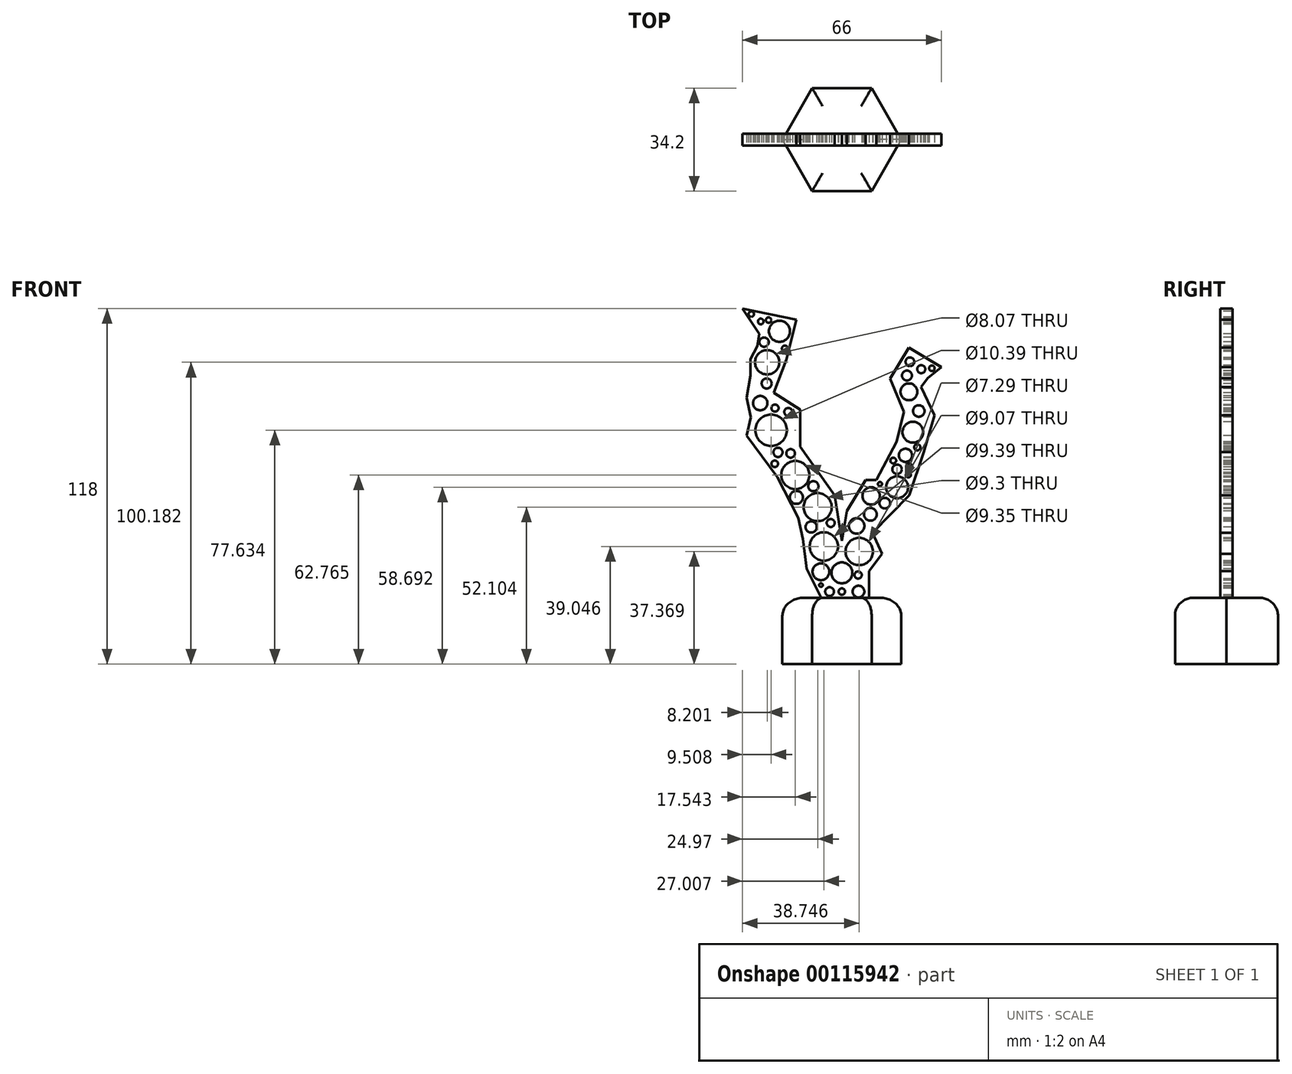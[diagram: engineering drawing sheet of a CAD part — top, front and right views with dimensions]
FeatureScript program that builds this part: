
annotation { "Feature Type Name" : "Feature", "Feature Type Description" : "" }
export const myFeature = defineFeature(function(context is Context, id is Id, definition is map)
    precondition{}
    {
        {
            var Q0;
            Q0=qCreatedBy(makeId("Top.planeOp"),FACE);
            var sketch = newSketch(context, id + "F0", { "sketchPlane" : qUnion([Q0])});
            skCircle(sketch, "E0.cCircle", {"center": v(0, 0) * mm, "radius": 17.1 * mm, "construction": true});
            skLineSegment(sketch, "E0.0", {"start": v(-9.87, 17.1) * mm, "end": v(9.87, 17.1) * mm});
            skLineSegment(sketch, "E0.1", {"start": v(9.87, 17.1) * mm, "end": v(19.74, 0) * mm});
            skLineSegment(sketch, "E0.2", {"start": v(19.74, 0) * mm, "end": v(9.87, -17.1) * mm});
            skLineSegment(sketch, "E0.3", {"start": v(9.87, -17.1) * mm, "end": v(-9.87, -17.1) * mm});
            skLineSegment(sketch, "E0.4", {"start": v(-9.87, -17.1) * mm, "end": v(-19.74, 0) * mm});
            skLineSegment(sketch, "E0.5", {"start": v(-19.74, 0) * mm, "end": v(-9.87, 17.1) * mm});
            skPoint(sketch, "E0.0.midPoint", {"position": v(0, 17.1) * mm});
            skSolve(sketch);
        }
        {
            var Q0;
            Q0 = qSketchRegion(id + "F0", true);
            extrude(context, id + "F1", {"entities" : qUnion([Q0]), "depth" : 22 * mm});
        }
        {
            var Q0;
            Q0=makeQuery(id+"F1.opExtrude","CAP_FACE",FACE,{"disambiguationData":[OSD([sQuery(id+"F0.wireOp",EDGE,"E0.0"),sQuery(id+"F0.wireOp",EDGE,"E0.1"),sQuery(id+"F0.wireOp",EDGE,"E0.2"),sQuery(id+"F0.wireOp",EDGE,"E0.3"),sQuery(id+"F0.wireOp",EDGE,"E0.4"),sQuery(id+"F0.wireOp",EDGE,"E0.5")])],"isStart":false});
            fillet(context, id + "F2", {"entities" : qUnion([Q0]), "radius" : 6 * mm, "tangentPropagation" : true, "allowEdgeOverflow" : false});
        }
        {
            var Q0;
            Q0=makeQuery(id+"F1.opExtrude","CAP_FACE",FACE,{"disambiguationData":[OSD([sQuery(id+"F0.wireOp",EDGE,"E0.0"),sQuery(id+"F0.wireOp",EDGE,"E0.1"),sQuery(id+"F0.wireOp",EDGE,"E0.2"),sQuery(id+"F0.wireOp",EDGE,"E0.3"),sQuery(id+"F0.wireOp",EDGE,"E0.4"),sQuery(id+"F0.wireOp",EDGE,"E0.5")])],"isStart":false});
            var sketch = newSketch(context, id + "F3", { "sketchPlane" : qUnion([Q0])});
            skLineSegment(sketch, "E1.bottom", {"start": v(-33, 2) * mm, "end": v(33, 2) * mm});
            skLineSegment(sketch, "E1.top", {"start": v(-33, -2) * mm, "end": v(33, -2) * mm});
            skLineSegment(sketch, "E1.left", {"start": v(-33, 2) * mm, "end": v(-33, -2) * mm});
            skLineSegment(sketch, "E1.right", {"start": v(33, 2) * mm, "end": v(33, -2) * mm});
            skPoint(sketch, "E1.middle", {"position": v(0, 0) * mm});
            skSolve(sketch);
        }
        {
            var Q0;
            Q0 = qSketchRegion(id + "F3", true);
            extrude(context, id + "F4", {"entities" : qUnion([Q0]), "operationType" : NewBodyOperationType.ADD, "depth" : 96 * mm});
        }
        {
            var Q0;
            Q0=makeQuery(id+"F4.opExtrude","SWEPT_FACE",FACE,{"disambiguationData":[OSD([sQuery(id+"F3.wireOp",EDGE,"E1.top")])]});
            var sketch = newSketch(context, id + "F5", { "sketchPlane" : qUnion([Q0])});
            skCircle(sketch, "E2", {"center": v(-15.46, 62.77) * mm, "radius": 4.67 * mm});
            skCircle(sketch, "E3", {"center": v(-8.03, 52.1) * mm, "radius": 4.65 * mm});
            skCircle(sketch, "E4", {"center": v(-6, 39.05) * mm, "radius": 4.7 * mm});
            skCircle(sketch, "E5", {"center": v(5.75, 37.37) * mm, "radius": 4.53 * mm});
            skCircle(sketch, "E6", {"center": v(4.9, 45.87) * mm, "radius": 2.58 * mm});
            skCircle(sketch, "E7", {"center": v(9.46, 49.7) * mm, "radius": 2.12 * mm});
            skCircle(sketch, "E8", {"center": v(9.7, 55.82) * mm, "radius": 2.88 * mm});
            skCircle(sketch, "E9", {"center": v(18.32, 58.7) * mm, "radius": 3.64 * mm});
            skCircle(sketch, "E10", {"center": v(18.32, 64.68) * mm, "radius": 1.56 * mm});
            skCircle(sketch, "E11", {"center": v(14.25, 53.42) * mm, "radius": 1.78 * mm});
            skCircle(sketch, "E12", {"center": v(-3.72, 46.83) * mm, "radius": 1.32 * mm});
            skCircle(sketch, "E13", {"center": v(-10.19, 45.52) * mm, "radius": 1.86 * mm});
            skCircle(sketch, "E14", {"center": v(-9.47, 59.05) * mm, "radius": 1.68 * mm});
            skCircle(sketch, "E15", {"center": v(-15.1, 55.34) * mm, "radius": 2.16 * mm});
            skCircle(sketch, "E16", {"center": v(-22.28, 66.48) * mm, "radius": 1.08 * mm});
            skCircle(sketch, "E17", {"center": v(-17.01, 69.95) * mm, "radius": 1.45 * mm});
            skCircle(sketch, "E18", {"center": v(-6.95, 30.66) * mm, "radius": 2.79 * mm});
            skCircle(sketch, "E19", {"center": v(0, 30.3) * mm, "radius": 3.46 * mm});
            skCircle(sketch, "E20", {"center": v(5.5, 24.07) * mm, "radius": 1.95 * mm});
            skCircle(sketch, "E21", {"center": v(5.39, 29.58) * mm, "radius": 1.2 * mm});
            skCircle(sketch, "E22", {"center": v(-4.08, 24.07) * mm, "radius": 1.46 * mm});
            skCircle(sketch, "E23", {"center": v(0, 24.07) * mm, "radius": 1.08 * mm});
            skCircle(sketch, "E24", {"center": v(-6.95, 26.23) * mm, "radius": 0.6 * mm});
            skLineSegment(sketch, "E25", {"start": v(-6.83, 22) * mm, "end": v(-11.66, 31.63) * mm});
            skLineSegment(sketch, "E26", {"start": v(-11.66, 31.63) * mm, "end": v(-12.94, 41.57) * mm});
            skLineSegment(sketch, "E27", {"start": v(-12.94, 41.57) * mm, "end": v(-14.5, 48.52) * mm});
            skLineSegment(sketch, "E28", {"start": v(-14.5, 48.52) * mm, "end": v(-21.45, 62.17) * mm});
            skLineSegment(sketch, "E29", {"start": v(-21.45, 62.17) * mm, "end": v(-31.63, 75.83) * mm});
            skLineSegment(sketch, "E30", {"start": v(10.18, 43.6) * mm, "end": v(13.3, 36.65) * mm});
            skLineSegment(sketch, "E31", {"start": v(13.3, 36.65) * mm, "end": v(8.98, 30.9) * mm});
            skLineSegment(sketch, "E32", {"start": v(8.98, 30.9) * mm, "end": v(8.98, 22) * mm});
            skCircle(sketch, "E33", {"center": v(-20.71, 110.48) * mm, "radius": 3.5 * mm});
            skCircle(sketch, "E34", {"center": v(-24.8, 100.18) * mm, "radius": 4.04 * mm});
            skCircle(sketch, "E35", {"center": v(-23.5, 77.63) * mm, "radius": 5.2 * mm});
            skCircle(sketch, "E36", {"center": v(-27.09, 86.62) * mm, "radius": 2.38 * mm});
            skCircle(sketch, "E37", {"center": v(21.11, 69.3) * mm, "radius": 2.2 * mm});
            skCircle(sketch, "E38", {"center": v(23.57, 76.98) * mm, "radius": 3.45 * mm});
            skCircle(sketch, "E39", {"center": v(22.26, 90.38) * mm, "radius": 2.8 * mm});
            skCircle(sketch, "E40", {"center": v(22.59, 100.35) * mm, "radius": 1.46 * mm});
            skCircle(sketch, "E41", {"center": v(26.34, 97.9) * mm, "radius": 1.35 * mm});
            skCircle(sketch, "E42", {"center": v(21.6, 95.77) * mm, "radius": 1.63 * mm});
            skCircle(sketch, "E43", {"center": v(25.53, 84) * mm, "radius": 1.91 * mm});
            skCircle(sketch, "E44", {"center": v(-24.96, 93.16) * mm, "radius": 1.67 * mm});
            skCircle(sketch, "E45", {"center": v(-17.77, 83.68) * mm, "radius": 1.35 * mm});
            skCircle(sketch, "E46", {"center": v(-21.2, 70.28) * mm, "radius": 1.52 * mm});
            skCircle(sketch, "E47", {"center": v(-22.18, 84.99) * mm, "radius": 1.19 * mm});
            skCircle(sketch, "E48", {"center": v(-18.92, 104.76) * mm, "radius": 0.98 * mm});
            skPoint(sketch, "E49.endSnap0", {"position": v(-11.68, 104.81) * mm});
            skPoint(sketch, "E50.orphan", {"position": v(-8.27, 100.32) * mm});
            skPoint(sketch, "E49.end.orphan", {"position": v(-11.68, 96.42) * mm});
            skPoint(sketch, "E51.end.orphan", {"position": v(0, 40.87) * mm});
            skLineSegment(sketch, "E52", {"start": v(0, 40.87) * mm, "end": v(1.67, 50.84) * mm});
            skLineSegment(sketch, "E53", {"start": v(1.67, 50.84) * mm, "end": v(7.88, 61.13) * mm});
            skLineSegment(sketch, "E54", {"start": v(7.88, 61.13) * mm, "end": v(11.47, 61.13) * mm});
            skLineSegment(sketch, "E55", {"start": v(11.47, 61.13) * mm, "end": v(18.17, 73.88) * mm});
            skLineSegment(sketch, "E56", {"start": v(18.17, 73.88) * mm, "end": v(20.62, 83.68) * mm});
            skLineSegment(sketch, "E57", {"start": v(20.62, 83.68) * mm, "end": v(16.05, 94.8) * mm});
            skLineSegment(sketch, "E58", {"start": v(16.05, 94.8) * mm, "end": v(22.26, 105.08) * mm});
            skLineSegment(sketch, "E59", {"start": v(22.26, 105.08) * mm, "end": v(33, 98.6) * mm});
            skLineSegment(sketch, "E60", {"start": v(33, 98.6) * mm, "end": v(28.47, 94.95) * mm});
            skLineSegment(sketch, "E61", {"start": v(28.47, 94.95) * mm, "end": v(26.34, 91.91) * mm});
            skLineSegment(sketch, "E62", {"start": v(26.34, 91.91) * mm, "end": v(30.73, 82.54) * mm});
            skPoint(sketch, "E62.endSnap0", {"position": v(30.73, 96.78) * mm});
            skLineSegment(sketch, "E63", {"start": v(30.73, 82.54) * mm, "end": v(27.12, 70.33) * mm});
            skLineSegment(sketch, "E64", {"start": v(27.12, 70.33) * mm, "end": v(22.33, 56.1) * mm});
            skLineSegment(sketch, "E65", {"start": v(22.33, 56.1) * mm, "end": v(10.18, 43.6) * mm});
            skLineSegment(sketch, "E66", {"start": v(-18.38, 101.07) * mm, "end": v(-22.6, 90) * mm});
            skLineSegment(sketch, "E67", {"start": v(-22.6, 90) * mm, "end": v(-13.86, 84.48) * mm});
            skLineSegment(sketch, "E68", {"start": v(-13.86, 84.48) * mm, "end": v(-13.86, 72.1) * mm});
            skLineSegment(sketch, "E69", {"start": v(-13.86, 72.1) * mm, "end": v(-2.36, 56.1) * mm});
            skLineSegment(sketch, "E70", {"start": v(-2.36, 56.1) * mm, "end": v(0, 40.87) * mm});
            skPoint(sketch, "E71.start.orphan", {"position": v(-15.1, 109.3) * mm});
            skPoint(sketch, "E72.start.orphan", {"position": v(-15.1, 110.48) * mm});
            skLineSegment(sketch, "E73", {"start": v(-18.38, 101.07) * mm, "end": v(-15.1, 114.38) * mm});
            skLineSegment(sketch, "E74", {"start": v(-15.1, 114.38) * mm, "end": v(-33, 118) * mm});
            skLineSegment(sketch, "E75", {"start": v(-33, 118) * mm, "end": v(-27.47, 109.58) * mm});
            skLineSegment(sketch, "E76", {"start": v(-27.47, 109.58) * mm, "end": v(-28.07, 105.56) * mm});
            skLineSegment(sketch, "E77", {"start": v(-28.07, 105.56) * mm, "end": v(-30.35, 101.2) * mm});
            skLineSegment(sketch, "E78", {"start": v(-30.35, 101.2) * mm, "end": v(-30.35, 95.84) * mm});
            skLineSegment(sketch, "E79", {"start": v(-30.35, 95.84) * mm, "end": v(-31.63, 88.42) * mm});
            skLineSegment(sketch, "E80", {"start": v(-31.63, 88.42) * mm, "end": v(-30.21, 81.96) * mm});
            skLineSegment(sketch, "E81", {"start": v(-30.21, 81.96) * mm, "end": v(-31.63, 75.83) * mm});
            skCircle(sketch, "E82", {"center": v(-30.08, 116.17) * mm, "radius": 0.9 * mm});
            skCircle(sketch, "E83", {"center": v(-26.93, 113.72) * mm, "radius": 0.94 * mm});
            skCircle(sketch, "E84", {"center": v(-24.32, 114.18) * mm, "radius": 0.9 * mm});
            skCircle(sketch, "E85", {"center": v(-25.82, 106.87) * mm, "radius": 1.55 * mm});
            skCircle(sketch, "E86", {"center": v(22.33, 65.55) * mm, "radius": 1.05 * mm});
            skCircle(sketch, "E87", {"center": v(17.04, 67.57) * mm, "radius": 0.96 * mm});
            skCircle(sketch, "E88", {"center": v(25.02, 71.97) * mm, "radius": 1.03 * mm});
            skCircle(sketch, "E89", {"center": v(22.09, 62.8) * mm, "radius": 0.83 * mm});
            skCircle(sketch, "E90", {"center": v(12.64, 59.77) * mm, "radius": 0.67 * mm});
            skCircle(sketch, "E91", {"center": v(29.88, 98.2) * mm, "radius": 0.92 * mm});
            skSolve(sketch);
        }
        {
            var Q0;
            Q0 = qSketchRegion(id + "F5", true);
            var Q1;
            {var subQ3=sQuery(id+"F5.wireOp",EDGE,"E25");Q1=makeQuery(id+"F5.imprint","IMPRINT",FACE,{"disambiguationData":[TD([[makeQuery(id+"F5.imprint","IMPRINT",EDGE,{"derivedFrom":subQ3}),1.0]])]});}
            var Q2;
            {var subQ0=sQuery(id+"F5.wireOp",EDGE,"CKBydIxl-e5yF-c1Wh-eSFo-G8iD2UtCF3KL");Q2=makeQuery(id+"F5.imprint","IMPRINT",FACE,{"disambiguationData":[TD([[makeQuery(id+"F5.imprint","IMPRINT",EDGE,{"derivedFrom":subQ0}),1.0]])]});}
            var Q3;
            {var subQ0=sQuery(id+"F5.wireOp",EDGE,"SzIdVFzJ-F6iO-mLX6-RHjo-YFIBbbv2dyrD");Q3=makeQuery(id+"F5.imprint","IMPRINT",FACE,{"disambiguationData":[TD([[makeQuery(id+"F5.imprint","IMPRINT",EDGE,{"derivedFrom":subQ0}),1.0]])]});}
            var Q4;
            Q4=makeQuery(id+"F5.imprint","IMPRINT",FACE,{"disambiguationData":[TD([[makeQuery(id+"F5.imprint","IMPRINT",EDGE,{"derivedFrom":sQuery(id+"F5.wireOp",EDGE,"E52")}),1.0]])]});
            var Q5;
            Q5=makeQuery(id+"F5.imprint","IMPRINT",FACE,{"disambiguationData":[TD([[makeQuery(id+"F5.imprint","IMPRINT",EDGE,{"derivedFrom":sQuery(id+"F5.wireOp",EDGE,"E30")}),1.0]])]});
            extrude(context, id + "F6", {"entities" : qUnion([Q0, Q1, Q2, Q3, Q4, Q5]), "operationType" : NewBodyOperationType.REMOVE, "endBound" : BoundingType.THROUGH_ALL, "oppositeDirection" : true, "depth" : 25 * mm});
        }
    });
